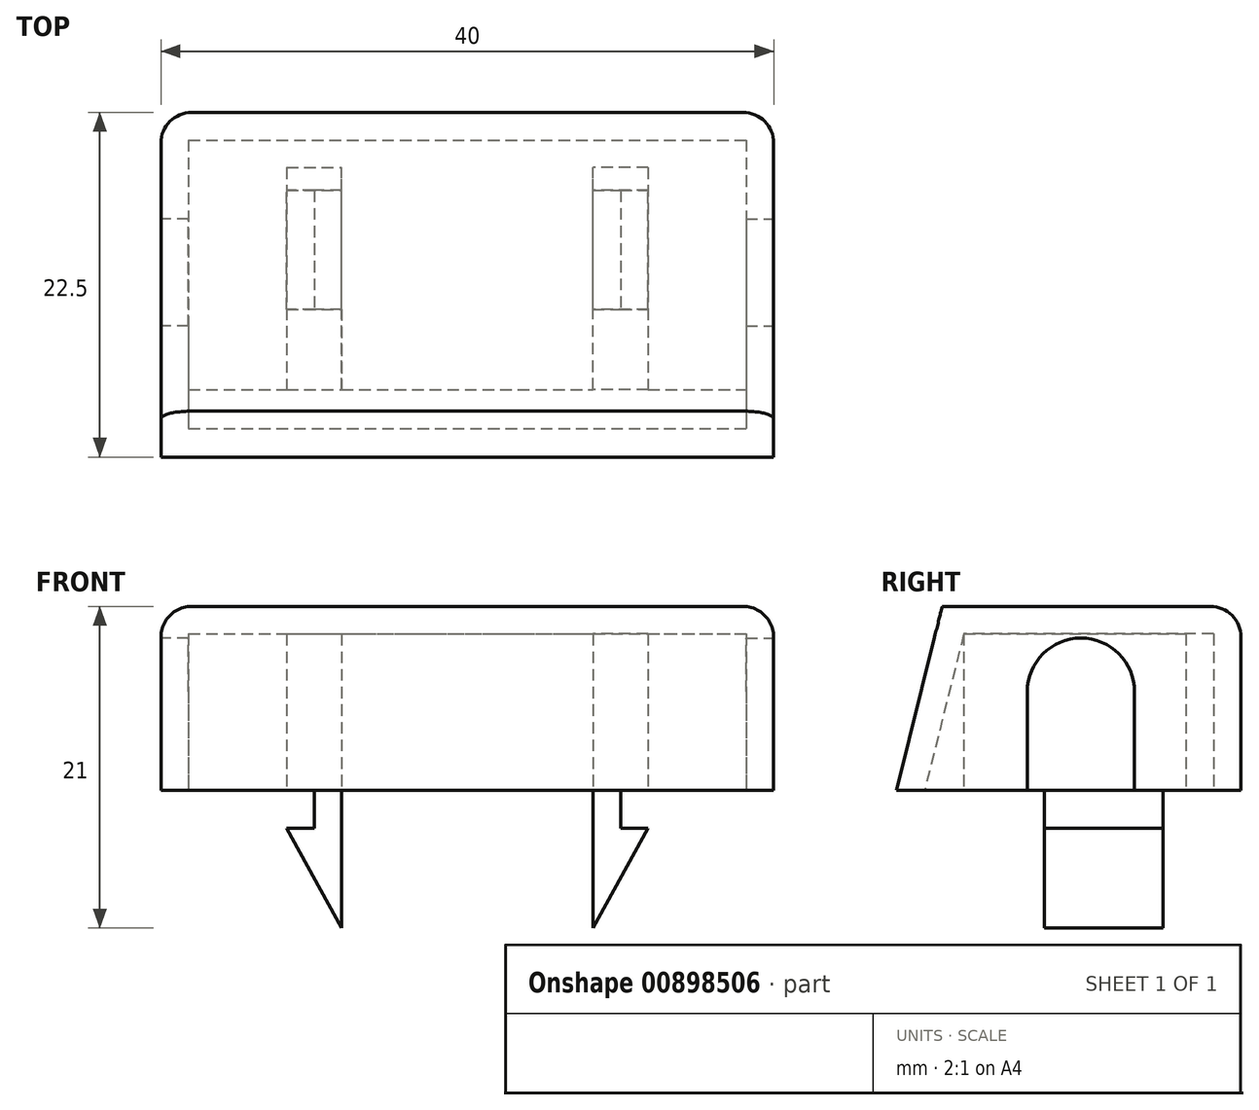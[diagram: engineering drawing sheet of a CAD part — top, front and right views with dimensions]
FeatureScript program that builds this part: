
annotation { "Feature Type Name" : "Feature", "Feature Type Description" : "" }
export const myFeature = defineFeature(function(context is Context, id is Id, definition is map)
    precondition{}
    {
        {
            var Q0;
            Q0=qCreatedBy(makeId("Top.planeOp"),FACE);
            var sketch = newSketch(context, id + "F0", { "sketchPlane" : qUnion([Q0])});
            skLineSegment(sketch, "E0.bottom", {"start": v(-22.14, 14.13) * mm, "end": v(17.86, 14.13) * mm});
            skLineSegment(sketch, "E0.top", {"start": v(-22.14, -8.37) * mm, "end": v(17.86, -8.37) * mm});
            skLineSegment(sketch, "E0.left", {"start": v(-22.14, 14.13) * mm, "end": v(-22.14, -8.37) * mm});
            skLineSegment(sketch, "E0.right", {"start": v(17.86, 14.13) * mm, "end": v(17.86, -8.37) * mm});
            skSolve(sketch);
        }
        {
            var Q0;
            Q0 = qSketchRegion(id + "F0", true);
            extrude(context, id + "F1", {"entities" : qUnion([Q0]), "depth" : 12 * mm, "offsetDistance" : 25 * mm});
        }
        {
            var Q0;
            Q0=makeQuery(id+"F1.opExtrude","SWEPT_FACE",FACE,{"disambiguationData":[OSD([sQuery(id+"F0.wireOp",EDGE,"E0.right")])]});
            var sketch = newSketch(context, id + "F2", { "sketchPlane" : qUnion([Q0])});
            skLineSegment(sketch, "E1", {"start": v(-8.37, 0) * mm, "end": v(-8.37, 12) * mm});
            skLineSegment(sketch, "E2", {"start": v(-8.37, 12) * mm, "end": v(-5.37, 12) * mm});
            skLineSegment(sketch, "E3", {"start": v(-5.37, 12) * mm, "end": v(-8.37, 0) * mm});
            skSolve(sketch);
        }
        {
            var Q0;
            Q0=makeQuery(id+"F2.imprint","IMPRINT",FACE,{"disambiguationData":[TD([[makeQuery(id+"F2.imprint","IMPRINT",EDGE,{"derivedFrom":sQuery(id+"F2.wireOp",EDGE,"E1")}),1.0]])]});
            extrude(context, id + "F3", {"entities" : qUnion([Q0]), "operationType" : NewBodyOperationType.REMOVE, "oppositeDirection" : true, "depth" : 40 * mm, "offsetDistance" : 25 * mm});
        }
        {
            var Q0;
            Q0=makeQuery(id+"F1.opExtrude","CAP_FACE",FACE,{"disambiguationData":[OSD([sQuery(id+"F0.wireOp",EDGE,"E0.bottom"),sQuery(id+"F0.wireOp",EDGE,"E0.top"),sQuery(id+"F0.wireOp",EDGE,"E0.left"),sQuery(id+"F0.wireOp",EDGE,"E0.right")])],"isStart":true});
            shell(context, id + "F4", {"entities" : qUnion([Q0]), "thickness" : 1.8 * mm});
        }
        {
            var Q0;
            Q0=makeQuery(id+"F4.opShell","OFFSET_FACE",FACE,{"disambiguationData":[OSD([sQuery(id+"F0.wireOp",EDGE,"E0.bottom"),sQuery(id+"F0.wireOp",EDGE,"E0.top"),sQuery(id+"F0.wireOp",EDGE,"E0.left"),sQuery(id+"F0.wireOp",EDGE,"E0.right")])]});
            var sketch = newSketch(context, id + "F5", { "sketchPlane" : qUnion([Q0])});
            skLineSegment(sketch, "E4", {"start": v(-10.34, 3.97) * mm, "end": v(-10.34, -10.53) * mm});
            skLineSegment(sketch, "E5", {"start": v(6.06, 3.97) * mm, "end": v(6.06, -10.53) * mm});
            skSolve(sketch);
        }
        {
            var Q0;
            Q0=sQuery(id+"F5.wireOp",EDGE,"E4");
            extrude(context, id + "F6", {"bodyType" : ToolBodyType.SURFACE, "surfaceEntities" : qUnion([Q0]), "depth" : 19.2 * mm, "offsetDistance" : 25 * mm});
        }
        {
            var Q0;
            Q0=makeQuery(id+"F6.opExtrude","SWEPT_FACE",FACE,{"disambiguationData":[OSD([sQuery(id+"F5.wireOp",EDGE,"E4")])]});
            extrude(context, id + "F7", {"entities" : qUnion([Q0]), "operationType" : NewBodyOperationType.ADD, "depth" : 3.6 * mm, "offsetDistance" : 25 * mm});
        }
        {
            var Q0;
            Q0=sQuery(id+"F5.wireOp",EDGE,"E5");
            extrude(context, id + "F8", {"bodyType" : ToolBodyType.SURFACE, "surfaceEntities" : qUnion([Q0]), "depth" : 19.2 * mm, "offsetDistance" : 25 * mm});
        }
        {
            var Q0;
            Q0=makeQuery(id+"F8.opExtrude","SWEPT_FACE",FACE,{"disambiguationData":[OSD([sQuery(id+"F5.wireOp",EDGE,"E5")])]});
            extrude(context, id + "F9", {"entities" : qUnion([Q0]), "operationType" : NewBodyOperationType.ADD, "depth" : -3.6 * mm, "offsetDistance" : 25 * mm});
        }
        {
            var Q0;
            Q0=makeQuery(id+"F9.opExtrude","CAP_FACE",FACE,{"disambiguationData":[OSD([sQuery(id+"F5.wireOp",EDGE,"E5")])],"isStart":false});
            var sketch = newSketch(context, id + "F10", { "sketchPlane" : qUnion([Q0])});
            skLineSegment(sketch, "E6", {"start": v(-3.97, -9) * mm, "end": v(1.28, -9) * mm});
            skLineSegment(sketch, "E7", {"start": v(1.28, -9) * mm, "end": v(1.28, 0) * mm});
            skLineSegment(sketch, "E8", {"start": v(1.28, 0) * mm, "end": v(-3.97, 0) * mm});
            skLineSegment(sketch, "E9", {"start": v(-3.97, 0) * mm, "end": v(-3.97, -9) * mm});
            skSolve(sketch);
        }
        {
            var Q0;
            Q0 = qSketchRegion(id + "F10", true);
            extrude(context, id + "F11", {"entities" : qUnion([Q0]), "operationType" : NewBodyOperationType.REMOVE, "oppositeDirection" : true, "depth" : 3.7 * mm, "offsetDistance" : 25 * mm});
        }
        {
            var Q0;
            Q0=makeQuery(id+"F7.opExtrude","CAP_FACE",FACE,{"disambiguationData":[OSD([sQuery(id+"F5.wireOp",EDGE,"E4")])],"isStart":false});
            var sketch = newSketch(context, id + "F12", { "sketchPlane" : qUnion([Q0])});
            skLineSegment(sketch, "E10", {"start": v(3.97, -9) * mm, "end": v(-1.28, -9) * mm});
            skLineSegment(sketch, "E11", {"start": v(-1.28, -9) * mm, "end": v(-1.28, 0) * mm});
            skLineSegment(sketch, "E12", {"start": v(-1.28, 0) * mm, "end": v(3.97, 0) * mm});
            skLineSegment(sketch, "E13", {"start": v(3.97, 0) * mm, "end": v(3.97, -9) * mm});
            skSolve(sketch);
        }
        {
            var Q0;
            Q0=makeQuery(id+"F12.imprint","IMPRINT",FACE,{"disambiguationData":[TD([[makeQuery(id+"F12.imprint","IMPRINT",EDGE,{"derivedFrom":sQuery(id+"F12.wireOp",EDGE,"E10")}),-1.0]])]});
            extrude(context, id + "F13", {"entities" : qUnion([Q0]), "operationType" : NewBodyOperationType.REMOVE, "oppositeDirection" : true, "depth" : 3.7 * mm, "offsetDistance" : 25 * mm});
        }
        {
            var Q0;
            Q0=makeQuery(id+"F9.opExtrude","CAP_FACE",FACE,{"disambiguationData":[OSD([sQuery(id+"F5.wireOp",EDGE,"E5")])],"isStart":false});
            var sketch = newSketch(context, id + "F14", { "sketchPlane" : qUnion([Q0])});
            skLineSegment(sketch, "E14.bottom", {"start": v(9.03, -9) * mm, "end": v(10.53, -9) * mm});
            skLineSegment(sketch, "E14.top", {"start": v(9.03, 0) * mm, "end": v(10.53, 0) * mm});
            skLineSegment(sketch, "E14.left", {"start": v(9.03, -9) * mm, "end": v(9.03, 0) * mm});
            skLineSegment(sketch, "E14.right", {"start": v(10.53, -9) * mm, "end": v(10.53, 0) * mm});
            skSolve(sketch);
        }
        {
            var Q0;
            Q0=makeQuery(id+"F14.imprint","IMPRINT",FACE,{"disambiguationData":[TD([[makeQuery(id+"F14.imprint","IMPRINT",EDGE,{"derivedFrom":sQuery(id+"F14.wireOp",EDGE,"E14.bottom")}),1.0]])]});
            extrude(context, id + "F15", {"entities" : qUnion([Q0]), "operationType" : NewBodyOperationType.REMOVE, "oppositeDirection" : true, "depth" : 3.6 * mm, "offsetDistance" : 25 * mm});
        }
        {
            var Q0;
            Q0=makeQuery(id+"F7.opExtrude","CAP_FACE",FACE,{"disambiguationData":[OSD([sQuery(id+"F5.wireOp",EDGE,"E4")])],"isStart":false});
            var sketch = newSketch(context, id + "F16", { "sketchPlane" : qUnion([Q0])});
            skLineSegment(sketch, "E15.bottom", {"start": v(-9.03, -9) * mm, "end": v(-10.53, -9) * mm});
            skLineSegment(sketch, "E15.top", {"start": v(-9.03, 0) * mm, "end": v(-10.53, 0) * mm});
            skLineSegment(sketch, "E15.left", {"start": v(-9.03, -9) * mm, "end": v(-9.03, 0) * mm});
            skLineSegment(sketch, "E15.right", {"start": v(-10.53, -9) * mm, "end": v(-10.53, 0) * mm});
            skSolve(sketch);
        }
        {
            var Q0;
            Q0=makeQuery(id+"F16.imprint","IMPRINT",FACE,{"disambiguationData":[TD([[makeQuery(id+"F16.imprint","IMPRINT",EDGE,{"derivedFrom":sQuery(id+"F16.wireOp",EDGE,"E15.bottom")}),-1.0]])]});
            extrude(context, id + "F17", {"entities" : qUnion([Q0]), "operationType" : NewBodyOperationType.REMOVE, "oppositeDirection" : true, "depth" : 3.6 * mm, "offsetDistance" : 25 * mm});
        }
        {
            var Q0;
            Q0=makeQuery(id+"F7.opExtrude","CAP_FACE",FACE,{"disambiguationData":[OSD([sQuery(id+"F5.wireOp",EDGE,"E4")])],"isStart":false});
            var sketch = newSketch(context, id + "F18", { "sketchPlane" : qUnion([Q0])});
            skLineSegment(sketch, "E16", {"start": v(-9.03, 0) * mm, "end": v(-1.28, 0) * mm});
            skLineSegment(sketch, "E17", {"start": v(-1.28, 0) * mm, "end": v(-1.28, -2.5) * mm});
            skLineSegment(sketch, "E18", {"start": v(-1.28, -2.5) * mm, "end": v(-9.03, -2.5) * mm});
            skPoint(sketch, "E18.endSnap0", {"position": v(-9.03, -4.5) * mm});
            skLineSegment(sketch, "E19", {"start": v(-9.03, -2.5) * mm, "end": v(-9.03, 0) * mm});
            skSolve(sketch);
        }
        {
            var Q0;
            Q0=makeQuery(id+"F18.imprint","IMPRINT",FACE,{"disambiguationData":[TD([[makeQuery(id+"F18.imprint","IMPRINT",EDGE,{"derivedFrom":sQuery(id+"F18.wireOp",EDGE,"E16")}),-1.0]])]});
            extrude(context, id + "F19", {"entities" : qUnion([Q0]), "operationType" : NewBodyOperationType.REMOVE, "oppositeDirection" : true, "depth" : 1.8 * mm, "offsetDistance" : 25 * mm});
        }
        {
            var Q0;
            Q0=makeQuery(id+"F9.opExtrude","CAP_FACE",FACE,{"disambiguationData":[OSD([sQuery(id+"F5.wireOp",EDGE,"E5")])],"isStart":false});
            var sketch = newSketch(context, id + "F20", { "sketchPlane" : qUnion([Q0])});
            skLineSegment(sketch, "E20", {"start": v(9.03, 0) * mm, "end": v(1.28, 0) * mm});
            skLineSegment(sketch, "E21", {"start": v(1.28, 0) * mm, "end": v(1.28, -2.5) * mm});
            skLineSegment(sketch, "E22", {"start": v(1.28, -2.5) * mm, "end": v(9.03, -2.5) * mm});
            skLineSegment(sketch, "E23", {"start": v(9.03, -2.5) * mm, "end": v(9.03, 0) * mm});
            skSolve(sketch);
        }
        {
            var Q0;
            Q0=makeQuery(id+"F20.imprint","IMPRINT",FACE,{"disambiguationData":[TD([[makeQuery(id+"F20.imprint","IMPRINT",EDGE,{"derivedFrom":sQuery(id+"F20.wireOp",EDGE,"E20")}),1.0]])]});
            extrude(context, id + "F21", {"entities" : qUnion([Q0]), "operationType" : NewBodyOperationType.REMOVE, "oppositeDirection" : true, "depth" : 1.8 * mm, "offsetDistance" : 25 * mm});
        }
        {
            var Q0;
            Q0=makeQuery(id+"F15.boolean.opBoolean","COPY",FACE,{"derivedFrom":makeQuery(id+"F15.opExtrude","SWEPT_FACE",FACE,{"disambiguationData":[OSD([sQuery(id+"F14.wireOp",EDGE,"E14.left")])]})});
            var sketch = newSketch(context, id + "F22", { "sketchPlane" : qUnion([Q0])});
            skLineSegment(sketch, "E24", {"start": v(-9.66, -2.5) * mm, "end": v(-6.06, -9) * mm});
            skSolve(sketch);
        }
        {
            var Q0;
            Q0=makeQuery(id+"F22.imprint","IMPRINT",FACE,{"disambiguationData":[TD([[makeQuery(id+"F22.imprint","IMPRINT",EDGE,{"derivedFrom":sQuery(id+"F22.wireOp",EDGE,"E24")}),-1.0]])]});
            extrude(context, id + "F23", {"entities" : qUnion([Q0]), "operationType" : NewBodyOperationType.REMOVE, "oppositeDirection" : true, "depth" : 7.75 * mm, "offsetDistance" : 25 * mm});
        }
        {
            var Q0;
            Q0=makeQuery(id+"F17.boolean.opBoolean","COPY",FACE,{"derivedFrom":makeQuery(id+"F17.opExtrude","SWEPT_FACE",FACE,{"disambiguationData":[OSD([sQuery(id+"F16.wireOp",EDGE,"E15.left")])]})});
            var sketch = newSketch(context, id + "F24", { "sketchPlane" : qUnion([Q0])});
            skLineSegment(sketch, "E25", {"start": v(13.94, -2.5) * mm, "end": v(10.34, -9) * mm});
            skSolve(sketch);
        }
        {
            var Q0;
            Q0=makeQuery(id+"F24.imprint","IMPRINT",FACE,{"disambiguationData":[TD([[makeQuery(id+"F24.imprint","IMPRINT",EDGE,{"derivedFrom":sQuery(id+"F24.wireOp",EDGE,"E25")}),1.0]])]});
            extrude(context, id + "F25", {"entities" : qUnion([Q0]), "operationType" : NewBodyOperationType.REMOVE, "oppositeDirection" : true, "depth" : 7.75 * mm, "offsetDistance" : 25 * mm});
        }
        {
            var Q0;
            Q0=makeQuery(id+"F1.opExtrude","SWEPT_FACE",FACE,{"disambiguationData":[OSD([sQuery(id+"F0.wireOp",EDGE,"E0.left")])]});
            var sketch = newSketch(context, id + "F26", { "sketchPlane" : qUnion([Q0])});
            skCircle(sketch, "E26", {"center": v(-3.68, 6.43) * mm, "radius": 3.5 * mm});
            skLineSegment(sketch, "E27", {"start": v(-7.18, 6.43) * mm, "end": v(-7.18, 0) * mm});
            skLineSegment(sketch, "E28", {"start": v(-0.18, 6.43) * mm, "end": v(-0.18, 0) * mm});
            skSolve(sketch);
        }
        {
            var Q0;
            {var subQ0=sQuery(id+"F26.wireOp",EDGE,"E27");Q0=makeQuery(id+"F26.imprint","IMPRINT",FACE,{"disambiguationData":[TD([[makeQuery(id+"F26.imprint","IMPRINT",EDGE,{"derivedFrom":subQ0}),1.0]])]});}
            var Q1;
            {var subQ0=sQuery(id+"F26.wireOp",EDGE,"E26");var subQ1=makeQuery(id+"F26.imprint","INTERSECT",VERTEX,{"derivedFrom":[subQ0,sQuery(id+"F26.wireOp",EDGE,"E27")]});Q1=makeQuery(id+"F26.imprint","IMPRINT",FACE,{"disambiguationData":[TD([[makeQuery(id+"F26.imprint","IMPRINT",EDGE,{"disambiguationData":[TD([[subQ1,1.0]])],"derivedFrom":subQ0}),1.0]])]});}
            extrude(context, id + "F27", {"entities" : qUnion([Q0, Q1]), "operationType" : NewBodyOperationType.REMOVE, "oppositeDirection" : true, "depth" : 1.8 * mm, "offsetDistance" : 25 * mm});
        }
        {
            var Q0;
            Q0=makeQuery(id+"F1.opExtrude","SWEPT_FACE",FACE,{"disambiguationData":[OSD([sQuery(id+"F0.wireOp",EDGE,"E0.right")])]});
            var sketch = newSketch(context, id + "F28", { "sketchPlane" : qUnion([Q0])});
            skCircle(sketch, "E29", {"center": v(3.68, 6.43) * mm, "radius": 3.5 * mm});
            skLineSegment(sketch, "E30", {"start": v(0.18, 6.43) * mm, "end": v(0.18, 0) * mm});
            skLineSegment(sketch, "E31", {"start": v(7.18, 6.43) * mm, "end": v(7.18, 0) * mm});
            skSolve(sketch);
        }
        {
            var Q0;
            {var subQ0=sQuery(id+"F28.wireOp",EDGE,"E29");var subQ1=makeQuery(id+"F28.imprint","INTERSECT",VERTEX,{"derivedFrom":[subQ0,sQuery(id+"F28.wireOp",EDGE,"E30")]});Q0=makeQuery(id+"F28.imprint","IMPRINT",FACE,{"disambiguationData":[TD([[makeQuery(id+"F28.imprint","IMPRINT",EDGE,{"disambiguationData":[TD([[subQ1,1.0]])],"derivedFrom":subQ0}),1.0]])]});}
            var Q1;
            {var subQ0=sQuery(id+"F28.wireOp",EDGE,"E30");Q1=makeQuery(id+"F28.imprint","IMPRINT",FACE,{"disambiguationData":[TD([[makeQuery(id+"F28.imprint","IMPRINT",EDGE,{"derivedFrom":subQ0}),1.0]])]});}
            extrude(context, id + "F29", {"entities" : qUnion([Q0, Q1]), "operationType" : NewBodyOperationType.REMOVE, "oppositeDirection" : true, "depth" : 1.8 * mm, "offsetDistance" : 25 * mm});
        }
        {
            var Q0;
            Q0=makeQuery(id+"F3.boolean.opBoolean","COPY",EDGE,{"derivedFrom":makeQuery(id+"F3.opExtrude","CAP_EDGE",EDGE,{"disambiguationData":[OSD([sQuery(id+"F2.wireOp",EDGE,"E3")])],"isStart":true})});
            var Q1;
            Q1=makeQuery(id+"F1.opExtrude","SWEPT_EDGE",EDGE,{"disambiguationData":[OSD([sQuery(id+"F0.wireOp",EDGE,"E0.bottom"),sQuery(id+"F0.wireOp",EDGE,"E0.right")])]});
            var Q2;
            Q2=makeQuery(id+"F1.opExtrude","CAP_EDGE",EDGE,{"disambiguationData":[OSD([sQuery(id+"F0.wireOp",EDGE,"E0.right")])],"isStart":false});
            var Q3;
            Q3=makeQuery(id+"F3.boolean.opBoolean","COPY",EDGE,{"derivedFrom":makeQuery(id+"F3.opExtrude","CAP_EDGE",EDGE,{"disambiguationData":[OSD([sQuery(id+"F2.wireOp",EDGE,"E3")])],"isStart":false})});
            var Q4;
            Q4=makeQuery(id+"F1.opExtrude","SWEPT_EDGE",EDGE,{"disambiguationData":[OSD([sQuery(id+"F0.wireOp",EDGE,"E0.bottom"),sQuery(id+"F0.wireOp",EDGE,"E0.left")])]});
            var Q5;
            Q5=makeQuery(id+"F1.opExtrude","CAP_EDGE",EDGE,{"disambiguationData":[OSD([sQuery(id+"F0.wireOp",EDGE,"E0.left")])],"isStart":false});
            var Q6;
            Q6=makeQuery(id+"F3.boolean.opBoolean","COPY",EDGE,{"derivedFrom":makeQuery(id+"F3.opExtrude","SWEPT_EDGE",EDGE,{"disambiguationData":[OSD([sQuery(id+"F0.wireOp",EDGE,"E0.right"),sQuery(id+"F2.wireOp",EDGE,"E2"),sQuery(id+"F2.wireOp",EDGE,"E3")])]})});
            var Q7;
            Q7=makeQuery(id+"F1.opExtrude","CAP_EDGE",EDGE,{"disambiguationData":[OSD([sQuery(id+"F0.wireOp",EDGE,"E0.bottom")])],"isStart":false});
            fillet(context, id + "F30", {"entities" : qUnion([Q0, Q1, Q2, Q3, Q4, Q5, Q6, Q7]), "radius" : 2 * mm, "tangentPropagation" : true, "allowEdgeOverflow" : false});
        }
    });
